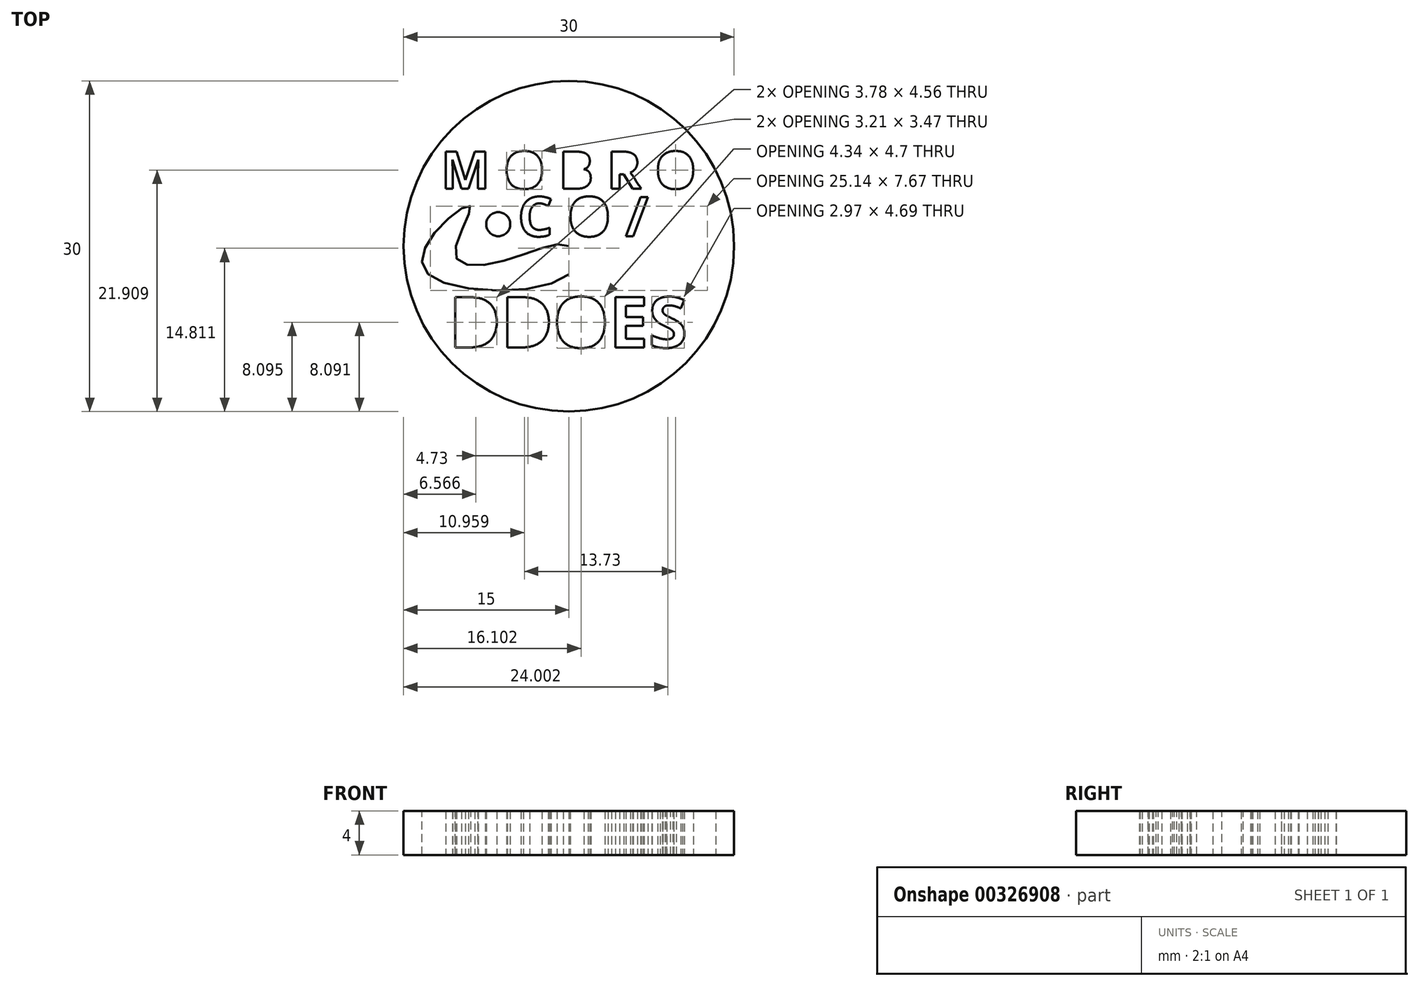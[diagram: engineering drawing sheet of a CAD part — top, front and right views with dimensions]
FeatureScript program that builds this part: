
annotation { "Feature Type Name" : "Feature", "Feature Type Description" : "" }
export const myFeature = defineFeature(function(context is Context, id is Id, definition is map)
    precondition{}
    {
        {
            var Q0;
            Q0=qCreatedBy(makeId("Top.planeOp"),FACE);
            var sketch = newSketch(context, id + "F0", { "sketchPlane" : qUnion([Q0])});
            skCircle(sketch, "E0", {"center": v(0, 0) * mm, "radius": 15 * mm});
            skLineSegment(sketch, "E1", {"start": v(0, 0) * mm, "end": v(0, -2.56) * mm});
            skFitSpline(sketch, "E2", {"points": [v(0, 0) * mm, v(5.77, -1.3) * mm, v(10.3, -0.79) * mm, v(8.92, 3.59) * mm, v(12.37, 0.98) * mm, v(12.44, -2.8) * mm, v(0, -2.56) * mm, v(0, 0) * mm]});
            skFitSpline(sketch, "E3.MirrorC", {"points": [v(0, 0) * mm, v(-5.77, -1.3) * mm, v(-10.3, -0.79) * mm, v(-8.92, 3.59) * mm, v(-12.37, 0.98) * mm, v(-12.44, -2.8) * mm, v(0, -2.56) * mm, v(0, 0) * mm]});
            skText(sketch, "E4", { "text": "M O B R O", "fontName": "OpenSans-Bold.ttf"});
            skText(sketch, "E5", { "text": "DDOES", "fontName": "OpenSans-Bold.ttf"});
            skText(sketch, "E6", { "text": "C O /", "fontName": "OpenSans-Bold.ttf"});
            skCircle(sketch, "E7", {"center": v(-6.4, 2) * mm, "radius": 1.1 * mm});
            skLineSegment(sketch, "E8", {"start": v(-4.63, 0.9) * mm, "end": v(-9.49, 0.9) * mm, "construction": true});
            skPoint(sketch, "E9", {"position": v(-1.08, 0.63) * mm});
            skLineSegment(sketch, "E10", {"start": v(7.5, 0.35) * mm, "end": v(0, 0.35) * mm, "construction": true});
            const initialGuessF0  = {"E4": [-0.0116, 0.00522, 1, 0, 0.0034], "E5": [-0.0109, -0.00919, 1, 0, 0.0046], "E6": [-0.00463, 0.0009, 1, 0, 0.0036]};
            skSetInitialGuess(sketch, initialGuessF0);
            skSolve(sketch);
        }
        {
            var Q0;
            Q0=qSketchRegion(id+"F0",true);
            extrude(context, id + "F1", {"entities" : qUnion([Q0]), "depth" : 4 * mm});
        }
    });
